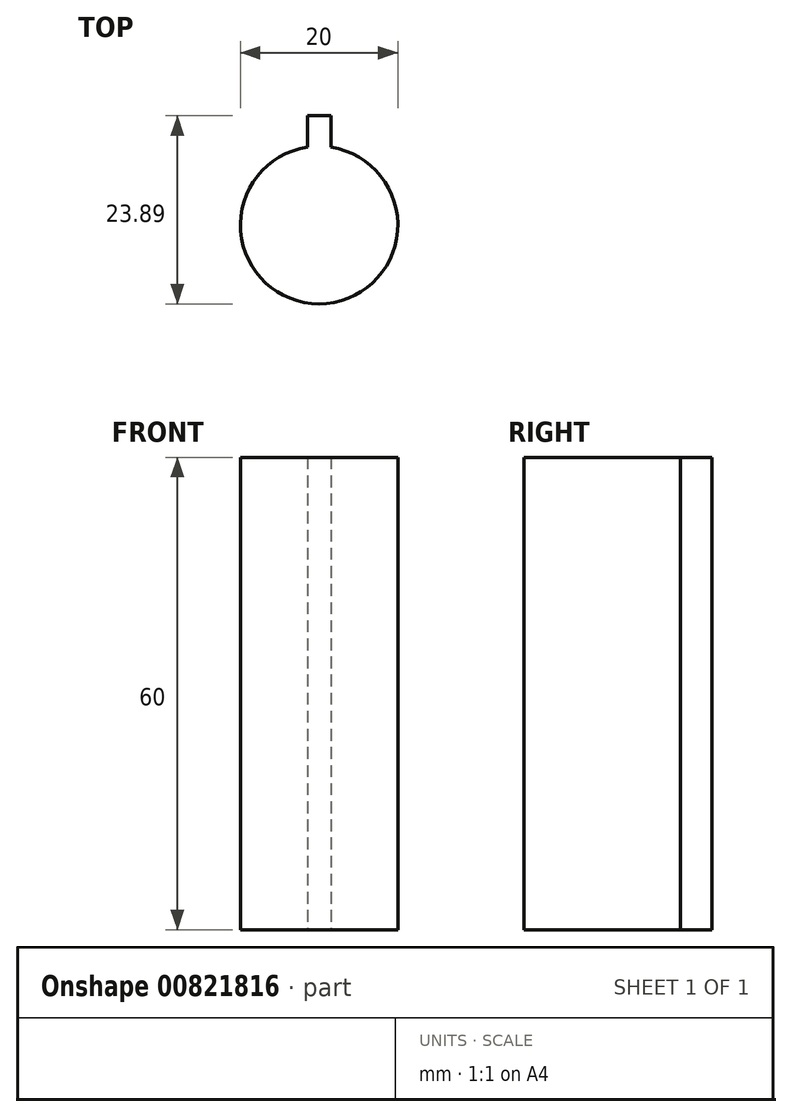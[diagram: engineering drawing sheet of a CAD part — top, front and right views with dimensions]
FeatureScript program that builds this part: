
annotation { "Feature Type Name" : "Feature", "Feature Type Description" : "" }
export const myFeature = defineFeature(function(context is Context, id is Id, definition is map)
    precondition{}
    {
        {
            var Q0;
            Q0=qCreatedBy(makeId("Top.planeOp"),FACE);
            var sketch = newSketch(context, id + "F0", { "sketchPlane" : qUnion([Q0])});
            skCircle(sketch, "E0", {"center": v(0, 0) * mm, "radius": 10 * mm});
            skLineSegment(sketch, "E1.top", {"start": v(-1.5, 13.89) * mm, "end": v(1.5, 13.89) * mm});
            skLineSegment(sketch, "E1.left", {"start": v(-1.5, 9.89) * mm, "end": v(-1.5, 13.89) * mm});
            skLineSegment(sketch, "E1.right", {"start": v(1.5, 9.89) * mm, "end": v(1.5, 13.89) * mm});
            skSolve(sketch);
        }
        {
            var Q0;
            Q0=makeQuery(id+"F0.imprint","IMPRINT",FACE,{"disambiguationData":[TD([[makeQuery(id+"F0.imprint","IMPRINT",EDGE,{"derivedFrom":sQuery(id+"F0.wireOp",EDGE,"E0")}),1.0]])]});
            var Q1;
            Q1=makeQuery(id+"F0.imprint","IMPRINT",FACE,{"disambiguationData":[TD([[makeQuery(id+"F0.imprint","IMPRINT",EDGE,{"derivedFrom":sQuery(id+"F0.wireOp",EDGE,"E1.top")}),-1.0]])]});
            extrude(context, id + "F1", {"entities" : qUnion([Q0, Q1]), "depth" : 60 * mm, "offsetDistance" : 25 * mm});
        }
    });
